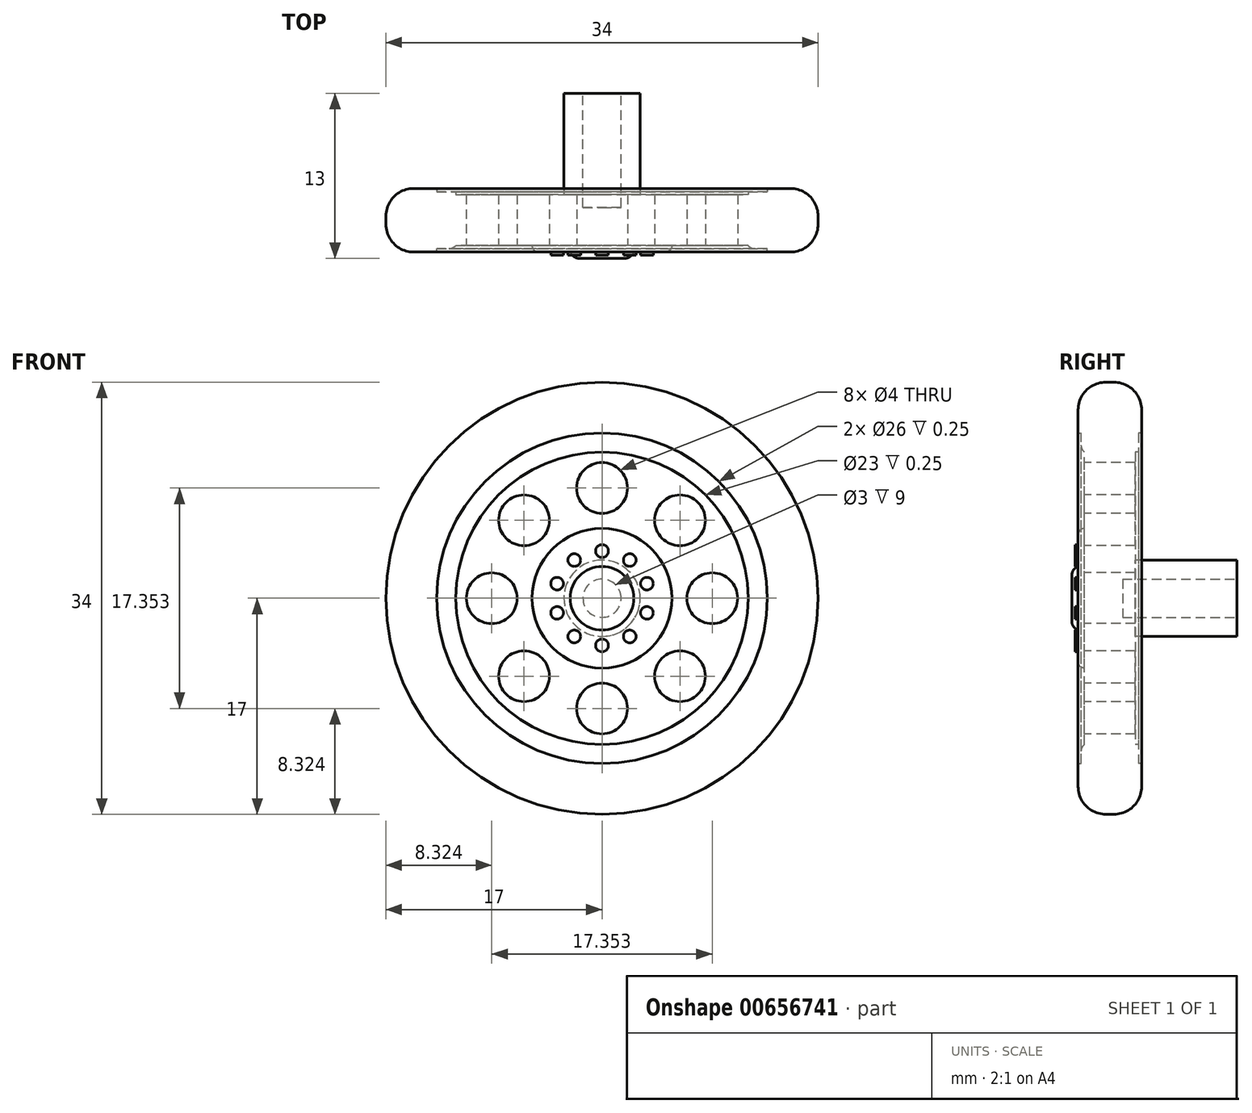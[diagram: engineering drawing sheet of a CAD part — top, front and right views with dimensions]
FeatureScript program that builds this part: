
annotation { "Feature Type Name" : "Feature", "Feature Type Description" : "" }
export const myFeature = defineFeature(function(context is Context, id is Id, definition is map)
    precondition{}
    {
        {
            var Q0;
            Q0=qCreatedBy(makeId("Front.planeOp"),FACE);
            var sketch = newSketch(context, id + "F0", { "sketchPlane" : qUnion([Q0])});
            skCircle(sketch, "E0", {"center": v(0, 0) * mm, "radius": 17 * mm});
            skSolve(sketch);
        }
        {
            var Q0;
            Q0=makeQuery(id+"F0.imprint","IMPRINT",FACE,{"disambiguationData":[TD([[makeQuery(id+"F0.imprint","IMPRINT",EDGE,{"derivedFrom":sQuery(id+"F0.wireOp",EDGE,"E0")}),1.0]])]});
            extrude(context, id + "F1", {"entities" : qUnion([Q0]), "depth" : 4 * mm, "offsetDistance" : 25 * mm});
        }
        {
            var Q0;
            Q0=makeQuery(id+"F1.opExtrude","CAP_FACE",FACE,{"disambiguationData":[OSD([sQuery(id+"F0.wireOp",EDGE,"E0")])],"isStart":false});
            var sketch = newSketch(context, id + "F2", { "sketchPlane" : qUnion([Q0])});
            skCircle(sketch, "E1", {"center": v(0, 8.68) * mm, "radius": 2 * mm});
            skCircle(sketch, "E2.1.0", {"center": v(-6.14, 6.14) * mm, "radius": 2 * mm});
            skCircle(sketch, "E2.2.0", {"center": v(-8.68, 0) * mm, "radius": 2 * mm});
            skPoint(sketch, "E2.center", {"position": v(0, 0) * mm});
            skCircle(sketch, "E3.1.3.0", {"center": v(-6.14, -6.14) * mm, "radius": 2 * mm});
            skCircle(sketch, "E3.1.4.0", {"center": v(0, -8.68) * mm, "radius": 2 * mm});
            skCircle(sketch, "E3.1.5.0", {"center": v(6.14, -6.14) * mm, "radius": 2 * mm});
            skCircle(sketch, "E3.1.6.0", {"center": v(8.68, 0) * mm, "radius": 2 * mm});
            skCircle(sketch, "E3.1.7.0", {"center": v(6.14, 6.14) * mm, "radius": 2 * mm});
            skSolve(sketch);
        }
        {
            var Q0;
            Q0=makeQuery(id+"F2.imprint","IMPRINT",FACE,{"disambiguationData":[TD([[makeQuery(id+"F2.imprint","IMPRINT",EDGE,{"derivedFrom":sQuery(id+"F2.wireOp",EDGE,"E1")}),1.0]])]});
            var Q1;
            Q1=makeQuery(id+"F2.imprint","IMPRINT",FACE,{"disambiguationData":[TD([[makeQuery(id+"F2.imprint","IMPRINT",EDGE,{"derivedFrom":sQuery(id+"F2.wireOp",EDGE,"E2.1.0")}),1.0]])]});
            var Q2;
            Q2=makeQuery(id+"F2.imprint","IMPRINT",FACE,{"disambiguationData":[TD([[makeQuery(id+"F2.imprint","IMPRINT",EDGE,{"derivedFrom":sQuery(id+"F2.wireOp",EDGE,"E2.2.0")}),1.0]])]});
            var Q3;
            Q3=makeQuery(id+"F2.imprint","IMPRINT",FACE,{"disambiguationData":[TD([[makeQuery(id+"F2.imprint","IMPRINT",EDGE,{"derivedFrom":sQuery(id+"F2.wireOp",EDGE,"E3.1.3.0")}),1.0]])]});
            var Q4;
            Q4=makeQuery(id+"F2.imprint","IMPRINT",FACE,{"disambiguationData":[TD([[makeQuery(id+"F2.imprint","IMPRINT",EDGE,{"derivedFrom":sQuery(id+"F2.wireOp",EDGE,"E3.1.4.0")}),1.0]])]});
            var Q5;
            Q5=makeQuery(id+"F2.imprint","IMPRINT",FACE,{"disambiguationData":[TD([[makeQuery(id+"F2.imprint","IMPRINT",EDGE,{"derivedFrom":sQuery(id+"F2.wireOp",EDGE,"E3.1.5.0")}),1.0]])]});
            var Q6;
            Q6=makeQuery(id+"F2.imprint","IMPRINT",FACE,{"disambiguationData":[TD([[makeQuery(id+"F2.imprint","IMPRINT",EDGE,{"derivedFrom":sQuery(id+"F2.wireOp",EDGE,"E3.1.6.0")}),1.0]])]});
            var Q7;
            Q7=makeQuery(id+"F2.imprint","IMPRINT",FACE,{"disambiguationData":[TD([[makeQuery(id+"F2.imprint","IMPRINT",EDGE,{"derivedFrom":sQuery(id+"F2.wireOp",EDGE,"E3.1.7.0")}),1.0]])]});
            extrude(context, id + "F3", {"entities" : qUnion([Q0, Q1, Q2, Q3, Q4, Q5, Q6, Q7]), "operationType" : NewBodyOperationType.REMOVE, "oppositeDirection" : true, "depth" : 25 * mm, "offsetDistance" : 25 * mm});
        }
        {
            var Q0;
            Q0=makeQuery(id+"F1.opExtrude","CAP_FACE",FACE,{"disambiguationData":[OSD([sQuery(id+"F0.wireOp",EDGE,"E0")])],"isStart":false});
            var sketch = newSketch(context, id + "F4", { "sketchPlane" : qUnion([Q0])});
            skCircle(sketch, "E4", {"center": v(0, 0) * mm, "radius": 13 * mm});
            skCircle(sketch, "E5", {"center": v(0, 0) * mm, "radius": 11.5 * mm});
            skSolve(sketch);
        }
        {
            var Q0;
            Q0=makeQuery(id+"F4.imprint","IMPRINT",FACE,{"disambiguationData":[TD([[makeQuery(id+"F4.imprint","IMPRINT",EDGE,{"derivedFrom":sQuery(id+"F4.wireOp",EDGE,"E5")}),1.0]])]});
            var sketch = newSketch(context, id + "F5", { "sketchPlane" : qUnion([Q0])});
            skCircle(sketch, "E6", {"center": v(0, 0) * mm, "radius": 5.5 * mm});
            skSolve(sketch);
        }
        {
            var Q0;
            Q0=makeQuery(id+"F5.imprint","IMPRINT",FACE,{"disambiguationData":[TD([[makeQuery(id+"F5.imprint","IMPRINT",EDGE,{"derivedFrom":sQuery(id+"F5.wireOp",EDGE,"E6")}),1.0]])]});
            extrude(context, id + "F6", {"entities" : qUnion([Q0]), "operationType" : NewBodyOperationType.ADD, "depth" : .5 * mm, "offsetDistance" : 25 * mm});
        }
        {
            var Q0;
            Q0=makeQuery(id+"F6.opExtrude","CAP_FACE",FACE,{"disambiguationData":[OSD([sQuery(id+"F5.wireOp",EDGE,"E6")])],"isStart":false});
            var sketch = newSketch(context, id + "F7", { "sketchPlane" : qUnion([Q0])});
            skCircle(sketch, "E7", {"center": v(0, 0) * mm, "radius": 2.5 * mm});
            skSolve(sketch);
        }
        {
            var Q0;
            Q0=makeQuery(id+"F7.imprint","IMPRINT",FACE,{"disambiguationData":[TD([[makeQuery(id+"F7.imprint","IMPRINT",EDGE,{"derivedFrom":sQuery(id+"F7.wireOp",EDGE,"E7")}),1.0]])]});
            extrude(context, id + "F8", {"entities" : qUnion([Q0]), "operationType" : NewBodyOperationType.ADD, "depth" : .5 * mm, "offsetDistance" : 25 * mm});
        }
        {
            var Q0;
            Q0=makeQuery(id+"F6.opExtrude","CAP_FACE",FACE,{"disambiguationData":[OSD([sQuery(id+"F5.wireOp",EDGE,"E6")])],"isStart":false});
            var sketch = newSketch(context, id + "F9", { "sketchPlane" : qUnion([Q0])});
            skCircle(sketch, "E8", {"center": v(0, 3.71) * mm, "radius": 0.5 * mm});
            skCircle(sketch, "E9.1.0", {"center": v(-2.18, 3) * mm, "radius": 0.5 * mm});
            skCircle(sketch, "E9.2.0", {"center": v(-3.53, 1.15) * mm, "radius": 0.5 * mm});
            skCircle(sketch, "E9.3.0", {"center": v(-3.53, -1.15) * mm, "radius": 0.5 * mm});
            skCircle(sketch, "E9.4.0", {"center": v(-2.18, -3) * mm, "radius": 0.5 * mm});
            skCircle(sketch, "E9.5.0", {"center": v(0, -3.71) * mm, "radius": 0.5 * mm});
            skCircle(sketch, "E9.6.0", {"center": v(2.18, -3) * mm, "radius": 0.5 * mm});
            skCircle(sketch, "E9.7.0", {"center": v(3.53, -1.15) * mm, "radius": 0.5 * mm});
            skCircle(sketch, "E9.8.0", {"center": v(3.53, 1.15) * mm, "radius": 0.5 * mm});
            skCircle(sketch, "E9.9.0", {"center": v(2.18, 3) * mm, "radius": 0.5 * mm});
            skPoint(sketch, "E9.center", {"position": v(0, 0) * mm});
            skSolve(sketch);
        }
        {
            var Q0;
            Q0=makeQuery(id+"F9.imprint","IMPRINT",FACE,{"disambiguationData":[TD([[makeQuery(id+"F9.imprint","IMPRINT",EDGE,{"derivedFrom":sQuery(id+"F9.wireOp",EDGE,"E8")}),1.0]])]});
            var Q1;
            Q1=makeQuery(id+"F9.imprint","IMPRINT",FACE,{"disambiguationData":[TD([[makeQuery(id+"F9.imprint","IMPRINT",EDGE,{"derivedFrom":sQuery(id+"F9.wireOp",EDGE,"E9.1.0")}),1.0]])]});
            var Q2;
            Q2=makeQuery(id+"F9.imprint","IMPRINT",FACE,{"disambiguationData":[TD([[makeQuery(id+"F9.imprint","IMPRINT",EDGE,{"derivedFrom":sQuery(id+"F9.wireOp",EDGE,"E9.2.0")}),1.0]])]});
            var Q3;
            Q3=makeQuery(id+"F9.imprint","IMPRINT",FACE,{"disambiguationData":[TD([[makeQuery(id+"F9.imprint","IMPRINT",EDGE,{"derivedFrom":sQuery(id+"F9.wireOp",EDGE,"E9.3.0")}),1.0]])]});
            var Q4;
            Q4=makeQuery(id+"F9.imprint","IMPRINT",FACE,{"disambiguationData":[TD([[makeQuery(id+"F9.imprint","IMPRINT",EDGE,{"derivedFrom":sQuery(id+"F9.wireOp",EDGE,"E9.4.0")}),1.0]])]});
            var Q5;
            Q5=makeQuery(id+"F9.imprint","IMPRINT",FACE,{"disambiguationData":[TD([[makeQuery(id+"F9.imprint","IMPRINT",EDGE,{"derivedFrom":sQuery(id+"F9.wireOp",EDGE,"E9.5.0")}),1.0]])]});
            var Q6;
            Q6=makeQuery(id+"F9.imprint","IMPRINT",FACE,{"disambiguationData":[TD([[makeQuery(id+"F9.imprint","IMPRINT",EDGE,{"derivedFrom":sQuery(id+"F9.wireOp",EDGE,"E9.6.0")}),1.0]])]});
            var Q7;
            Q7=makeQuery(id+"F9.imprint","IMPRINT",FACE,{"disambiguationData":[TD([[makeQuery(id+"F9.imprint","IMPRINT",EDGE,{"derivedFrom":sQuery(id+"F9.wireOp",EDGE,"E9.7.0")}),1.0]])]});
            var Q8;
            Q8=makeQuery(id+"F9.imprint","IMPRINT",FACE,{"disambiguationData":[TD([[makeQuery(id+"F9.imprint","IMPRINT",EDGE,{"derivedFrom":sQuery(id+"F9.wireOp",EDGE,"E9.8.0")}),1.0]])]});
            var Q9;
            Q9=makeQuery(id+"F9.imprint","IMPRINT",FACE,{"disambiguationData":[TD([[makeQuery(id+"F9.imprint","IMPRINT",EDGE,{"derivedFrom":sQuery(id+"F9.wireOp",EDGE,"E9.9.0")}),1.0]])]});
            extrude(context, id + "F10", {"entities" : qUnion([Q0, Q1, Q2, Q3, Q4, Q5, Q6, Q7, Q8, Q9]), "operationType" : NewBodyOperationType.ADD, "depth" : .25 * mm, "offsetDistance" : 25 * mm});
        }
        {
            var Q0;
            Q0=makeQuery(id+"F1.opExtrude","CAP_FACE",FACE,{"disambiguationData":[OSD([sQuery(id+"F0.wireOp",EDGE,"E0")])],"isStart":true});
            var sketch = newSketch(context, id + "F11", { "sketchPlane" : qUnion([Q0])});
            skCircle(sketch, "E10", {"center": v(0, 0) * mm, "radius": 13 * mm});
            skCircle(sketch, "E11", {"center": v(0, 0) * mm, "radius": 11.5 * mm});
            skSolve(sketch);
        }
        {
            var Q0;
            Q0=makeQuery(id+"F11.imprint","IMPRINT",FACE,{"disambiguationData":[TD([[makeQuery(id+"F11.imprint","IMPRINT",EDGE,{"derivedFrom":sQuery(id+"F11.wireOp",EDGE,"E10")}),-1.0]])]});
            extrude(context, id + "F12", {"entities" : qUnion([Q0]), "operationType" : NewBodyOperationType.ADD, "depth" : .5 * mm, "offsetDistance" : 25 * mm});
        }
        {
            var Q0;
            Q0=makeQuery(id+"F1.opExtrude","CAP_FACE",FACE,{"disambiguationData":[OSD([sQuery(id+"F0.wireOp",EDGE,"E0")])],"isStart":true});
            var sketch = newSketch(context, id + "F13", { "sketchPlane" : qUnion([Q0])});
            skCircle(sketch, "E12", {"center": v(0, 0) * mm, "radius": 11.5 * mm});
            skSolve(sketch);
        }
        {
            var Q0;
            Q0=makeQuery(id+"F13.imprint","IMPRINT",FACE,{"disambiguationData":[TD([[makeQuery(id+"F13.imprint","IMPRINT",EDGE,{"derivedFrom":sQuery(id+"F13.wireOp",EDGE,"E12")}),-1.0]])]});
            extrude(context, id + "F14", {"entities" : qUnion([Q0]), "operationType" : NewBodyOperationType.ADD, "depth" : .25 * mm, "offsetDistance" : 25 * mm});
        }
        {
            var Q0;
            Q0=makeQuery(id+"F4.imprint","IMPRINT",FACE,{"disambiguationData":[TD([[makeQuery(id+"F4.imprint","IMPRINT",EDGE,{"derivedFrom":sQuery(id+"F4.wireOp",EDGE,"E4")}),-1.0]])]});
            extrude(context, id + "F15", {"entities" : qUnion([Q0]), "operationType" : NewBodyOperationType.ADD, "depth" : .5 * mm, "offsetDistance" : 25 * mm});
        }
        {
            var Q0;
            Q0=makeQuery(id+"F1.opExtrude","CAP_FACE",FACE,{"disambiguationData":[OSD([sQuery(id+"F0.wireOp",EDGE,"E0")])],"isStart":false});
            var sketch = newSketch(context, id + "F16", { "sketchPlane" : qUnion([Q0])});
            skCircle(sketch, "E13", {"center": v(0, 0) * mm, "radius": 11.5 * mm});
            skSolve(sketch);
        }
        {
            var Q0;
            Q0=makeQuery(id+"F16.imprint","IMPRINT",FACE,{"disambiguationData":[TD([[makeQuery(id+"F16.imprint","IMPRINT",EDGE,{"derivedFrom":sQuery(id+"F16.wireOp",EDGE,"E13")}),-1.0]])]});
            extrude(context, id + "F17", {"entities" : qUnion([Q0]), "operationType" : NewBodyOperationType.ADD, "depth" : .25 * mm, "offsetDistance" : 25 * mm});
        }
        {
            var Q0;
            Q0=makeQuery(id+"F15.opExtrude","CAP_EDGE",EDGE,{"disambiguationData":[OSD([sQuery(id+"F0.wireOp",EDGE,"E0")])],"isStart":false});
            var Q1;
            {var subQ0=sQuery(id+"F0.wireOp",EDGE,"E0");Q1=makeQuery(id+"F15.boolean.opBoolean","MERGE",FACE,{"derivedFrom":[makeQuery(id+"F12.boolean.opBoolean","MERGE",FACE,{"derivedFrom":[makeQuery(id+"F1.opExtrude","SWEPT_FACE",FACE,{"disambiguationData":[OSD([subQ0])]}),makeQuery(id+"F12.opExtrude","SWEPT_FACE",FACE,{"disambiguationData":[OSD([subQ0])]})]}),makeQuery(id+"F15.opExtrude","SWEPT_FACE",FACE,{"disambiguationData":[OSD([subQ0])]})]});}
            fillet(context, id + "F18", {"entities" : qUnion([Q0, Q1]), "radius" : 2.17 * mm, "tangentPropagation" : true, "allowEdgeOverflow" : false});
        }
        {
            var Q0;
            Q0=makeQuery(id+"F1.opExtrude","CAP_FACE",FACE,{"disambiguationData":[OSD([sQuery(id+"F0.wireOp",EDGE,"E0")])],"isStart":true});
            var sketch = newSketch(context, id + "F19", { "sketchPlane" : qUnion([Q0])});
            skCircle(sketch, "E14", {"center": v(0, 0) * mm, "radius": 3 * mm});
            skSolve(sketch);
        }
        {
            var Q0;
            Q0=makeQuery(id+"F19.imprint","IMPRINT",FACE,{"disambiguationData":[TD([[makeQuery(id+"F19.imprint","IMPRINT",EDGE,{"derivedFrom":sQuery(id+"F19.wireOp",EDGE,"E14")}),1.0]])]});
            extrude(context, id + "F20", {"entities" : qUnion([Q0]), "operationType" : NewBodyOperationType.ADD, "depth" : 8 * mm, "offsetDistance" : 25 * mm});
        }
        {
            var Q0;
            Q0=makeQuery(id+"F20.opExtrude","CAP_FACE",FACE,{"disambiguationData":[OSD([sQuery(id+"F19.wireOp",EDGE,"E14")])],"isStart":false});
            var sketch = newSketch(context, id + "F21", { "sketchPlane" : qUnion([Q0])});
            skCircle(sketch, "E15", {"center": v(0, 0) * mm, "radius": 1.5 * mm});
            skSolve(sketch);
        }
        {
            var Q0;
            Q0=makeQuery(id+"F21.imprint","IMPRINT",FACE,{"disambiguationData":[TD([[makeQuery(id+"F21.imprint","IMPRINT",EDGE,{"derivedFrom":sQuery(id+"F21.wireOp",EDGE,"E15")}),1.0]])]});
            extrude(context, id + "F22", {"entities" : qUnion([Q0]), "operationType" : NewBodyOperationType.REMOVE, "oppositeDirection" : true, "depth" : 9 * mm, "offsetDistance" : 25 * mm});
        }
        {
            var Q0;
            Q0=makeQuery(id+"F8.opExtrude","CAP_EDGE",EDGE,{"disambiguationData":[OSD([sQuery(id+"F7.wireOp",EDGE,"E7")])],"isStart":false});
            fillet(context, id + "F23", {"entities" : qUnion([Q0]), "radius" : .75 * mm, "tangentPropagation" : true, "allowEdgeOverflow" : false});
        }
        {
            var Q0;
            Q0=makeQuery(id+"F6.opExtrude","CAP_EDGE",EDGE,{"disambiguationData":[OSD([sQuery(id+"F5.wireOp",EDGE,"E6")])],"isStart":false});
            fillet(context, id + "F24", {"entities" : qUnion([Q0]), "radius" : .5 * mm, "tangentPropagation" : true, "allowEdgeOverflow" : false});
        }
        {
            var Q0;
            Q0=makeQuery(id+"F17.opExtrude","CAP_EDGE",EDGE,{"disambiguationData":[OSD([sQuery(id+"F16.wireOp",EDGE,"E13")])],"isStart":false});
            fillet(context, id + "F25", {"entities" : qUnion([Q0]), "radius" : .75 * mm, "tangentPropagation" : true, "allowEdgeOverflow" : false});
        }
    });
